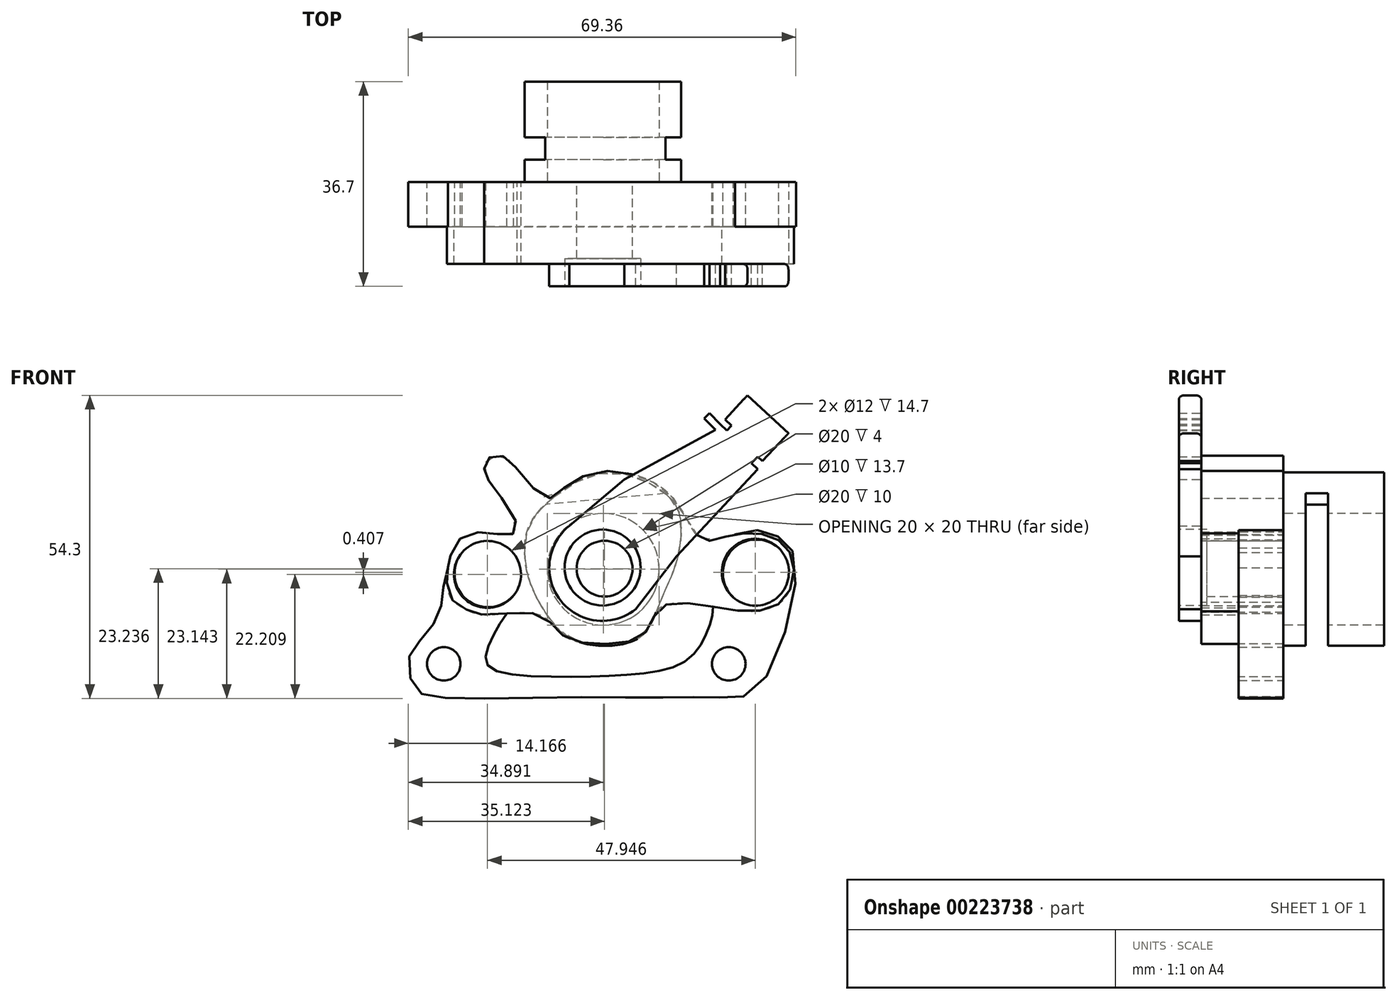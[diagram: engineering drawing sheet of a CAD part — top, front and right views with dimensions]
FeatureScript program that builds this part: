
annotation { "Feature Type Name" : "Feature", "Feature Type Description" : "" }
export const myFeature = defineFeature(function(context is Context, id is Id, definition is map)
    precondition{}
    {
        {
            var Q0;
            Q0=qCreatedBy(makeId("Front.planeOp"),FACE);
            var sketch = newSketch(context, id + "F0", { "sketchPlane" : qUnion([Q0])});
            skPoint(sketch, "E0.visualSharp", {"position": v(0, 0) * mm});
            skCircle(sketch, "E1", {"center": v(14.18, 22.16) * mm, "radius": 6 * mm});
            skCircle(sketch, "E2", {"center": v(62.18, 22.27) * mm, "radius": 6 * mm});
            skCircle(sketch, "E3", {"center": v(6.25, 6) * mm, "radius": 3 * mm});
            skCircle(sketch, "E4", {"center": v(57.25, 6) * mm, "radius": 3 * mm});
            skFitSpline(sketch, "E5", {"points": [v(5.2, 0) * mm, v(27.33, 0) * mm, v(46.83, 0) * mm, v(55.6, 0) * mm, v(62.39, 1.68) * mm, v(69.23, 23.64) * mm, v(66.34, 28.61) * mm, v(61.2, 29.95) * mm, v(55.97, 27) * mm, v(54.48, 19.37) * mm, v(54.37, 15.2) * mm, v(53.14, 11.14) * mm, v(49.5, 6.49) * mm, v(40.74, 4.19) * mm, v(25.35, 3.7) * mm, v(14.13, 5.74) * mm, v(14.6, 10.07) * mm, v(18.24, 15.9) * mm, v(21.45, 20.17) * mm, v(20.49, 25.83) * mm, v(15.04, 29.2) * mm, v(9.58, 27.76) * mm, v(6.97, 23.05) * mm, v(6, 18.67) * mm, v(5.3, 14.77) * mm, v(2.1, 10.28) * mm, v(0, 7.02) * mm, v(1.09, 1.68) * mm, v(5.2, 0) * mm]});
            skSolve(sketch);
        }
        {
            var Q0;
            Q0=qSketchRegion(id+"F0",true);
            extrude(context, id + "F1", {"entities" : qUnion([Q0]), "depth" : 8 * mm});
        }
        {
            var Q0;
            Q0=qCreatedBy(makeId("Front.planeOp"),FACE);
            var sketch = newSketch(context, id + "F2", { "sketchPlane" : qUnion([Q0])});
            skCircle(sketch, "E6", {"center": v(14.07, 22.02) * mm, "radius": 6 * mm});
            skCircle(sketch, "E7", {"center": v(62.01, 22.43) * mm, "radius": 6 * mm});
            skCircle(sketch, "E8", {"center": v(35.02, 23.05) * mm, "radius": 5 * mm});
            skFitSpline(sketch, "E9", {"points": [v(13.63, 14.78) * mm, v(23.3, 14.82) * mm, v(27.65, 11.05) * mm, v(35.52, 9.56) * mm, v(42.3, 11.54) * mm, v(44.9, 16.04) * mm, v(52.46, 16.57) * mm, v(61.94, 15.45) * mm, v(67.38, 17.88) * mm, v(68.86, 23.86) * mm, v(66.48, 27.94) * mm, v(61.72, 29.38) * mm, v(56.41, 28.7) * mm, v(52.46, 28.26) * mm, v(48.77, 33.65) * mm, v(43.34, 38.7) * mm, v(34.31, 40.48) * mm, v(27.6, 37.35) * mm, v(24.57, 35.7) * mm, v(18.5, 41.91) * mm, v(16.2, 43.3) * mm, v(13.8, 42.48) * mm, v(13.66, 40.07) * mm, v(15.19, 37.59) * mm, v(19.38, 30.4) * mm, v(17.92, 29.07) * mm, v(13.6, 29.58) * mm, v(8.9, 28.18) * mm, v(7.12, 24.05) * mm, v(7, 22.9) * mm, v(7.18, 18.4) * mm, v(10.04, 15.85) * mm, v(13.63, 14.78) * mm]});
            skSolve(sketch);
        }
        {
            var Q0;
            Q0=qSketchRegion(id+"F2",true);
            extrude(context, id + "F3", {"entities" : qUnion([Q0]), "operationType" : NewBodyOperationType.ADD, "depth" : 14.7 * mm});
        }
        {
            var Q0;
            Q0=makeQuery(id+"F3.opExtrude","CAP_FACE",FACE,{"disambiguationData":[OSD([sQuery(id+"F2.wireOp",EDGE,"E6"),sQuery(id+"F2.wireOp",EDGE,"E7"),sQuery(id+"F2.wireOp",EDGE,"E8"),sQuery(id+"F2.wireOp",EDGE,"E9")])],"isStart":false});
            cPlane(context, id + "F4", {"entities" : qUnion([Q0]), "cplaneType" : CPlaneType.OFFSET, "offset" : 0 * mm, "width" : 150 * mm, "height" : 150 * mm});
        }
        {
            var Q0;
            Q0=qCreatedBy(id+"F4.planeOp",FACE);
            var sketch = newSketch(context, id + "F5", { "sketchPlane" : qUnion([Q0])});
            skLineSegment(sketch, "E10", {"start": v(28.72, 30.72) * mm, "end": v(40.62, 15.78) * mm});
            skLineSegment(sketch, "E11", {"start": v(40.62, 15.78) * mm, "end": v(47.89, 25.27) * mm});
            skLineSegment(sketch, "E12", {"start": v(47.89, 25.27) * mm, "end": v(62.41, 40.9) * mm});
            skLineSegment(sketch, "E13", {"start": v(62.41, 40.9) * mm, "end": v(61.3, 41.93) * mm});
            skLineSegment(sketch, "E14", {"start": v(61.3, 41.93) * mm, "end": v(62.41, 43.12) * mm});
            skLineSegment(sketch, "E15", {"start": v(62.41, 43.12) * mm, "end": v(63.3, 42.3) * mm});
            skLineSegment(sketch, "E16", {"start": v(63.3, 42.3) * mm, "end": v(67.93, 47.3) * mm});
            skLineSegment(sketch, "E17", {"start": v(67.93, 47.3) * mm, "end": v(60.6, 54.1) * mm});
            skLineSegment(sketch, "E18", {"start": v(60.6, 54.1) * mm, "end": v(56.59, 49.78) * mm});
            skLineSegment(sketch, "E19", {"start": v(56.59, 49.78) * mm, "end": v(57.75, 48.7) * mm});
            skLineSegment(sketch, "E20", {"start": v(57.75, 48.7) * mm, "end": v(56.91, 47.8) * mm});
            skLineSegment(sketch, "E21", {"start": v(56.91, 47.8) * mm, "end": v(55.7, 48.92) * mm});
            skLineSegment(sketch, "E22", {"start": v(55.7, 48.92) * mm, "end": v(53.82, 50.9) * mm});
            skLineSegment(sketch, "E23", {"start": v(53.82, 50.9) * mm, "end": v(52.87, 49.98) * mm});
            skLineSegment(sketch, "E24", {"start": v(52.87, 49.98) * mm, "end": v(54.85, 47.9) * mm});
            skLineSegment(sketch, "E25", {"start": v(54.85, 47.9) * mm, "end": v(38.58, 39.01) * mm});
            skLineSegment(sketch, "E26", {"start": v(38.58, 39.01) * mm, "end": v(28.72, 30.72) * mm});
            skArc(sketch, "E27", {"start": v(28.72, 30.72) * mm, "mid": v(27.2, 17.3) * mm, "end": v(40.62, 15.78) * mm});
            skSolve(sketch);
        }
        {
            var Q0;
            Q0=qSketchRegion(id+"F5",true);
            extrude(context, id + "F6", {"entities" : qUnion([Q0]), "operationType" : NewBodyOperationType.ADD, "depth" : 4 * mm});
        }
        {
            var Q0;
            Q0=makeQuery(id+"F6.opExtrude","CAP_FACE",FACE,{"disambiguationData":[OSD([sQuery(id+"F5.wireOp",EDGE,"E11"),sQuery(id+"F5.wireOp",EDGE,"E12"),sQuery(id+"F5.wireOp",EDGE,"E13"),sQuery(id+"F5.wireOp",EDGE,"E14"),sQuery(id+"F5.wireOp",EDGE,"E15"),sQuery(id+"F5.wireOp",EDGE,"E16"),sQuery(id+"F5.wireOp",EDGE,"E17"),sQuery(id+"F5.wireOp",EDGE,"E18"),sQuery(id+"F5.wireOp",EDGE,"E19"),sQuery(id+"F5.wireOp",EDGE,"E20"),sQuery(id+"F5.wireOp",EDGE,"E21"),sQuery(id+"F5.wireOp",EDGE,"E22"),sQuery(id+"F5.wireOp",EDGE,"E23"),sQuery(id+"F5.wireOp",EDGE,"E24"),sQuery(id+"F5.wireOp",EDGE,"E25"),sQuery(id+"F5.wireOp",EDGE,"E26"),sQuery(id+"F5.wireOp",EDGE,"E27")])],"isStart":false});
            var sketch = newSketch(context, id + "F7", { "sketchPlane" : qUnion([Q0])});
            skCircle(sketch, "E28", {"center": v(34.67, 23.25) * mm, "radius": 6.8 * mm});
            skSolve(sketch);
        }
        {
            var Q0;
            Q0=makeQuery(id+"F7.imprint","IMPRINT",FACE,{"disambiguationData":[TD([[makeQuery(id+"F7.imprint","IMPRINT",EDGE,{"derivedFrom":sQuery(id+"F7.wireOp",EDGE,"E28")}),1.0]])]});
            var Q1;
            Q1=sQuery(id+"F7.wireOp",EDGE,"E28");
            extrude(context, id + "F8", {"entities" : qUnion([Q0]), "operationType" : NewBodyOperationType.REMOVE, "surfaceEntities" : qUnion([Q1]), "oppositeDirection" : true, "depth" : 5 * mm});
        }
        {
            var Q0;
            Q0=qCreatedBy(makeId("Front.planeOp"),FACE);
            var sketch = newSketch(context, id + "F9", { "sketchPlane" : qUnion([Q0])});
            skCircle(sketch, "E29", {"center": v(34.8, 22.95) * mm, "radius": 10 * mm});
            skFitSpline(sketch, "E30", {"points": [v(25.98, 35.9) * mm, v(35.32, 40.27) * mm, v(44.9, 37.28) * mm, v(48.49, 32.64) * mm, v(47.85, 24.15) * mm, v(45.76, 19) * mm, v(43.77, 14.18) * mm, v(40.18, 10.14) * mm, v(29.44, 10.31) * mm, v(24.17, 15.63) * mm, v(21.39, 21.5) * mm, v(21.2, 29.9) * mm, v(25.98, 35.9) * mm]});
            skSolve(sketch);
        }
        {
            var Q0;
            Q0=qSketchRegion(id+"F9",true);
            extrude(context, id + "F10", {"entities" : qUnion([Q0]), "operationType" : NewBodyOperationType.ADD, "oppositeDirection" : true, "depth" : 18 * mm});
        }
        {
            var Q0;
            Q0=makeQuery(id+"F10.opExtrude","CAP_FACE",FACE,{"disambiguationData":[OSD([sQuery(id+"F9.wireOp",EDGE,"E29"),sQuery(id+"F9.wireOp",EDGE,"E30")])],"isStart":false});
            cPlane(context, id + "F11", {"entities" : qUnion([Q0]), "cplaneType" : CPlaneType.OFFSET, "offset" : 10 * mm, "oppositeDirection" : true, "width" : 150 * mm, "height" : 150 * mm});
        }
        {
            var Q0;
            Q0=qCreatedBy(id+"F11.planeOp",FACE);
            var sketch = newSketch(context, id + "F12", { "sketchPlane" : qUnion([Q0])});
            skLineSegment(sketch, "E31", {"start": v(-51, 37) * mm, "end": v(-19.1, 34.06) * mm});
            skLineSegment(sketch, "E32", {"start": v(-19.1, 34.06) * mm, "end": v(-21.52, 7.78) * mm});
            skLineSegment(sketch, "E33", {"start": v(-21.52, 7.78) * mm, "end": v(-48.57, 7.86) * mm});
            skLineSegment(sketch, "E34", {"start": v(-48.57, 7.86) * mm, "end": v(-51, 37) * mm});
            skSolve(sketch);
        }
        {
            var Q0;
            Q0=qSketchRegion(id+"F12",true);
            extrude(context, id + "F13", {"entities" : qUnion([Q0]), "operationType" : NewBodyOperationType.REMOVE, "oppositeDirection" : true, "depth" : 4 * mm});
        }
        {
            var Q0;
            Q0=makeQuery(id+"F6.opExtrude","CAP_EDGE",EDGE,{"disambiguationData":[OSD([sQuery(id+"F5.wireOp",EDGE,"E17")])],"isStart":false});
            var Q1;
            Q1=makeQuery(id+"F6.opExtrude","CAP_EDGE",EDGE,{"disambiguationData":[OSD([sQuery(id+"F5.wireOp",EDGE,"E17")])],"isStart":true});
            fillet(context, id + "F14", {"entities" : qUnion([Q0, Q1]), "radius" : 1 * mm, "tangentPropagation" : true, "allowEdgeOverflow" : false});
        }
    });
